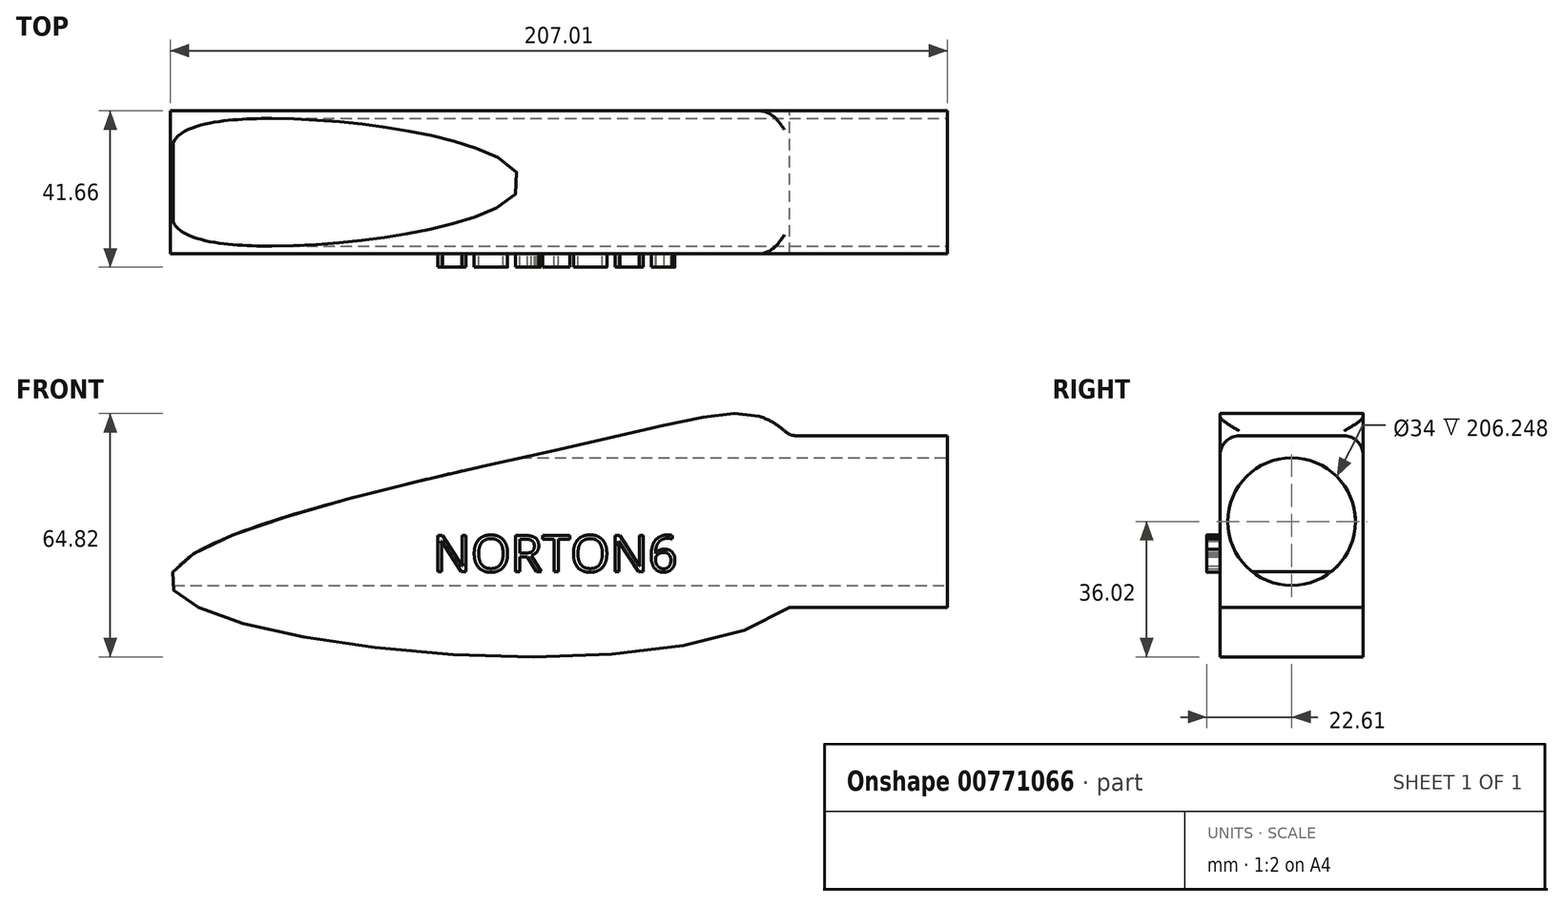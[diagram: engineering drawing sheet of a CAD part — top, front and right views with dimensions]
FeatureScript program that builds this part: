
annotation { "Feature Type Name" : "Feature", "Feature Type Description" : "" }
export const myFeature = defineFeature(function(context is Context, id is Id, definition is map)
    precondition{}
    {
        {
            var Q0;
            Q0=qCreatedBy(makeId("Front.planeOp"),FACE);
            var sketch = newSketch(context, id + "F0", { "sketchPlane" : qUnion([Q0])});
            skFitSpline(sketch, "E0", {"points": [v(-164.65, 5.63) * mm, v(-43.1, 46.22) * mm, v(0, 45.68) * mm, v(0, 0) * mm, v(-164.65, 5.63) * mm]});
            skLineSegment(sketch, "E1.bottom", {"start": v(0, 45.68) * mm, "end": v(42.05, 45.68) * mm});
            skLineSegment(sketch, "E1.top", {"start": v(0, 0) * mm, "end": v(42.05, 0) * mm});
            skLineSegment(sketch, "E1.left", {"start": v(0, 45.68) * mm, "end": v(0, 0) * mm});
            skLineSegment(sketch, "E1.right", {"start": v(42.05, 45.68) * mm, "end": v(42.05, 0) * mm});
            skPoint(sketch, "E2", {"position": v(-119.3, 28.42) * mm});
            skPoint(sketch, "E3", {"position": v(-119.3, -9.54) * mm});
            skSolve(sketch);
        }
        {
            var Q0;
            {var subQ1=sQuery(id+"F0.wireOp",EDGE,"E1.bottom");Q0=makeQuery(id+"F0.imprint","IMPRINT",FACE,{"disambiguationData":[TD([[makeQuery(id+"F0.imprint","IMPRINT",EDGE,{"derivedFrom":subQ1}),-1.0]])]});}
            var Q1;
            {var subQ0=sQuery(id+"F0.wireOp",EDGE,"E1.left");Q1=makeQuery(id+"F0.imprint","IMPRINT",FACE,{"disambiguationData":[TD([[makeQuery(id+"F0.imprint","IMPRINT",EDGE,{"derivedFrom":subQ0}),1.0]])]});}
            var Q2;
            {var subQ0=sQuery(id+"F0.wireOp",EDGE,"E1.left");Q2=makeQuery(id+"F0.imprint","IMPRINT",FACE,{"disambiguationData":[TD([[makeQuery(id+"F0.imprint","IMPRINT",EDGE,{"derivedFrom":subQ0}),-1.0]])]});}
            extrude(context, id + "F1", {"entities" : qUnion([Q0, Q1, Q2]), "depth" : 38.1 * mm, "offsetDistance" : 25.4 * mm});
        }
        {
            var Q0;
            Q0=makeQuery(id+"F1.opExtrude","SWEPT_FACE",FACE,{"disambiguationData":[OSD([sQuery(id+"F0.wireOp",EDGE,"E1.right")])]});
            var sketch = newSketch(context, id + "F2", { "sketchPlane" : qUnion([Q0])});
            skCircle(sketch, "E4", {"center": v(-19.05, 22.84) * mm, "radius": 17 * mm});
            skPoint(sketch, "E4.centerSnap0", {"position": v(-38.1, 22.84) * mm});
            skPoint(sketch, "E4.centerSnap1", {"position": v(-19.05, 45.68) * mm});
            skSolve(sketch);
        }
        {
            var Q0;
            Q0 = qSketchRegion(id + "F2", true);
            extrude(context, id + "F3", {"entities" : qUnion([Q0]), "operationType" : NewBodyOperationType.REMOVE, "oppositeDirection" : true, "depth" : 206.25 * mm, "offsetDistance" : 25.4 * mm});
        }
        {
            var Q0;
            Q0=makeQuery(id+"F1.opExtrude","CAP_FACE",FACE,{"disambiguationData":[OSD([sQuery(id+"F0.wireOp",EDGE,"E0"),sQuery(id+"F0.wireOp",EDGE,"E1.bottom"),sQuery(id+"F0.wireOp",EDGE,"E1.top"),sQuery(id+"F0.wireOp",EDGE,"E1.right")])],"isStart":false});
            var sketch = newSketch(context, id + "F4", { "sketchPlane" : qUnion([Q0])});
            skText(sketch, "E5", { "text": "NORTON6", "fontName": "OpenSans-Regular.ttf"});
            const initialGuessF4  = {"E5": [-0.09505, 0.00948, 1, 0, 0.00976]};
            skSetInitialGuess(sketch, initialGuessF4);
            skSolve(sketch);
        }
        {
            var Q0;
            Q0 = qSketchRegion(id + "F4", true);
            extrude(context, id + "F5", {"entities" : qUnion([Q0]), "operationType" : NewBodyOperationType.ADD, "depth" : 3.56 * mm, "offsetDistance" : 25.4 * mm});
        }
        {
            var Q0;
            Q0=makeQuery(id+"F1.opExtrude","CAP_EDGE",EDGE,{"disambiguationData":[OSD([sQuery(id+"F0.wireOp",EDGE,"E1.bottom")])],"isStart":false});
            var Q1;
            Q1=makeQuery(id+"F1.opExtrude","SWEPT_EDGE",EDGE,{"disambiguationData":[OSD([sQuery(id+"F0.wireOp",EDGE,"E0"),sQuery(id+"F0.wireOp",EDGE,"E1.bottom"),sQuery(id+"F0.wireOp",EDGE,"E1.left")])]});
            var Q2;
            Q2=makeQuery(id+"F1.opExtrude","CAP_EDGE",EDGE,{"disambiguationData":[OSD([sQuery(id+"F0.wireOp",EDGE,"E1.bottom")])],"isStart":true});
            fillet(context, id + "F6", {"entities" : qUnion([Q0, Q1, Q2]), "radius" : 5.08 * mm, "tangentPropagation" : true, "allowEdgeOverflow" : false});
        }
    });
